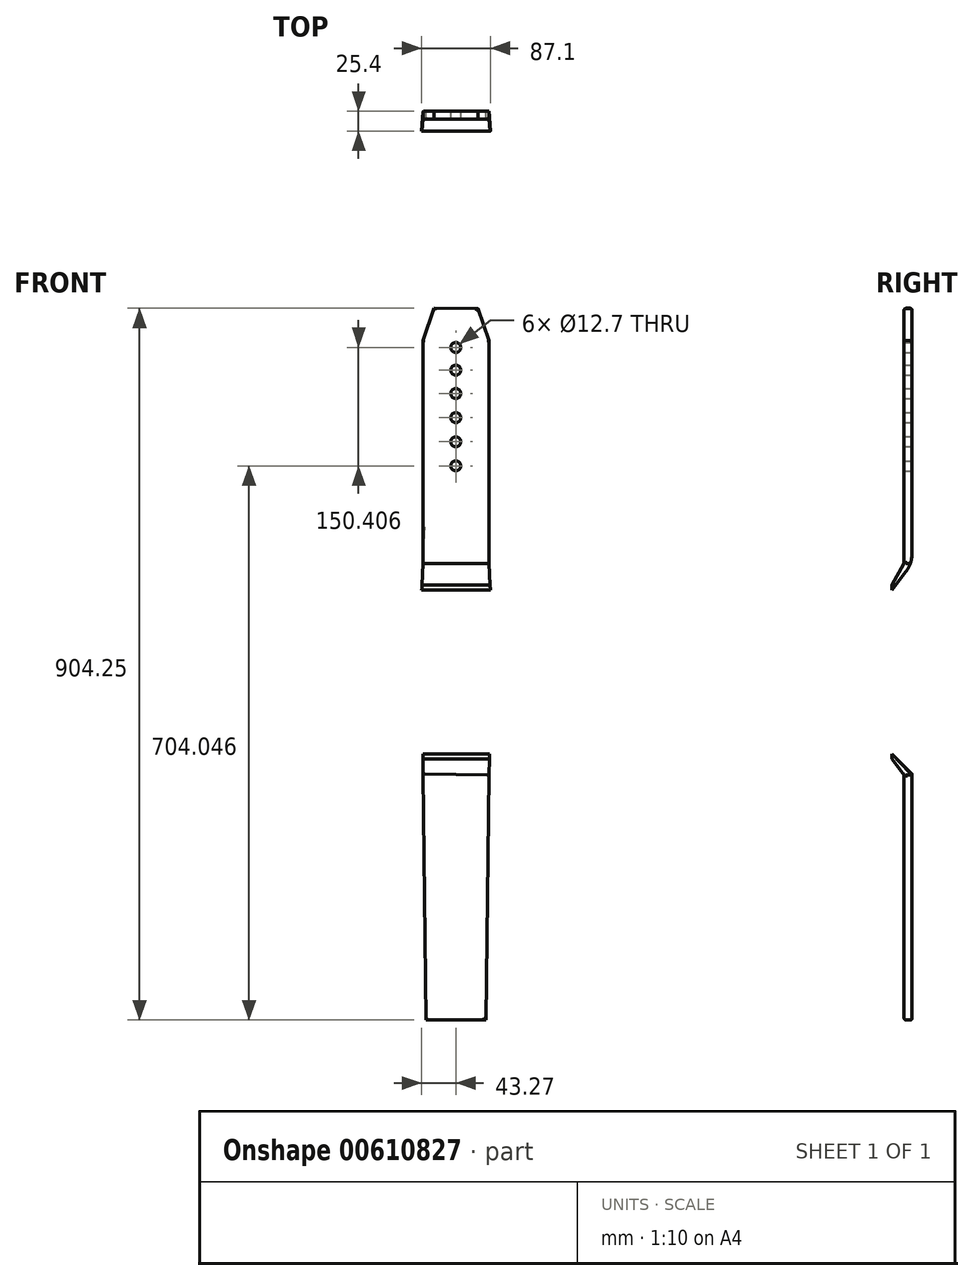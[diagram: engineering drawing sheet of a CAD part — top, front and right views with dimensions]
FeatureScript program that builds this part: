
annotation { "Feature Type Name" : "Feature", "Feature Type Description" : "" }
export const myFeature = defineFeature(function(context is Context, id is Id, definition is map)
    precondition{}
    {
        {
            var Q0;
            Q0=qCreatedBy(makeId("Front.planeOp"),FACE);
            cPlane(context, id + "F0", {"entities" : qUnion([Q0]), "cplaneType" : CPlaneType.OFFSET, "offset" : 17.78 * mm, "oppositeDirection" : true, "width" : 152.4 * mm, "height" : 152.4 * mm});
        }
        {
            var Q0;
            Q0=qCreatedBy(id+"F0.planeOp",FACE);
            var sketch = newSketch(context, id + "F1", { "sketchPlane" : qUnion([Q0])});
            skLineSegment(sketch, "E0.0", {"start": v(-43.1, 101.93) * mm, "end": v(43.66, 101.93) * mm});
            skFitSpline(sketch, "E1.0", {"points": [v(43.66, 101.93) * mm, v(43.72, 99.53) * mm, v(43.79, 97.13) * mm, v(43.86, 94.73) * mm]});
            skLineSegment(sketch, "E2.0", {"start": v(43.83, 95.64) * mm, "end": v(-43.27, 95.64) * mm});
            skFitSpline(sketch, "E3.0", {"points": [v(-43.3, 94.73) * mm, v(-43.22, 97.13) * mm, v(-43.16, 99.53) * mm, v(-43.1, 101.93) * mm]});
            skLineSegment(sketch, "E4.0", {"start": v(42.54, -118.99) * mm, "end": v(-41.97, -118.99) * mm});
            skLineSegment(sketch, "E5.0", {"start": v(-41.97, -112.7) * mm, "end": v(42.54, -112.7) * mm});
            skLineSegment(sketch, "E6.0", {"start": v(-41.97, -118.99) * mm, "end": v(-41.97, -112.7) * mm});
            skLineSegment(sketch, "E7.0", {"start": v(42.54, -112.7) * mm, "end": v(42.54, -118.99) * mm});
            skSolve(sketch);
        }
        {
            var Q0;
            Q0=qCreatedBy(id+"F0.planeOp",FACE);
            cPlane(context, id + "F2", {"entities" : qUnion([Q0]), "cplaneType" : CPlaneType.OFFSET, "offset" : 25.4 * mm, "oppositeDirection" : true, "width" : 152.4 * mm, "height" : 152.4 * mm});
        }
        {
            var Q0;
            Q0=qCreatedBy(id+"F2.planeOp",FACE);
            var sketch = newSketch(context, id + "F3", { "sketchPlane" : qUnion([Q0])});
            skLineSegment(sketch, "E8", {"start": v(42.35, 129.12) * mm, "end": v(-41.73, 129.12) * mm});
            skPoint(sketch, "E9.end.orphan", {"position": v(33.41, 331.77) * mm});
            skPoint(sketch, "E10.end.orphan", {"position": v(-33.96, 331.77) * mm});
            skLineSegment(sketch, "E11", {"start": v(0, 453.24) * mm, "end": v(-27.94, 453.36) * mm});
            skLineSegment(sketch, "E12", {"start": v(-27.94, 453.36) * mm, "end": v(0, 453.24) * mm});
            skLineSegment(sketch, "E13", {"start": v(0, 453.24) * mm, "end": v(27.94, 453.13) * mm});
            skLineSegment(sketch, "E14", {"start": v(42.35, 129.12) * mm, "end": v(42.35, 412.45) * mm});
            skLineSegment(sketch, "E15", {"start": v(-41.73, 129.12) * mm, "end": v(-41.73, 412.45) * mm});
            skLineSegment(sketch, "E16", {"start": v(27.94, 453.13) * mm, "end": v(42.35, 412.45) * mm});
            skLineSegment(sketch, "E17", {"start": v(-27.94, 453.36) * mm, "end": v(-41.73, 412.45) * mm});
            skSolve(sketch);
        }
        {
            var Q0;
            Q0 = qSketchRegion(id + "F3", true);
            extrude(context, id + "F4", {"entities" : qUnion([Q0]), "depth" : 10.16 * mm, "offsetDistance" : 25.4 * mm});
        }
        {
            var Q1;
            Q1=makeQuery(id+"F1.imprint","IMPRINT",FACE,{"disambiguationData":[TD([[makeQuery(id+"F1.imprint","IMPRINT",EDGE,{"derivedFrom":sQuery(id+"F1.wireOp",EDGE,"E0.0")}),-1.0]])]});
            var Q2;
            Q2=makeQuery(id+"F4.opExtrude","SWEPT_FACE",FACE,{"disambiguationData":[OSD([sQuery(id+"F3.wireOp",EDGE,"E8")])]});
            loft(context, id + "F5", {"operationType" : NewBodyOperationType.ADD, "sheetProfilesArray" : [{ "sheetProfileEntities" : qUnion([Q1]) }, { "sheetProfileEntities" : qUnion([Q2]) }]});
        }
        {
            var Q0;
            Q0=qCreatedBy(id+"F2.planeOp",FACE);
            var sketch = newSketch(context, id + "F6", { "sketchPlane" : qUnion([Q0])});
            skLineSegment(sketch, "E18", {"start": v(0, -450.9) * mm, "end": v(-38.1, -450.9) * mm});
            skLineSegment(sketch, "E19", {"start": v(0, -450.9) * mm, "end": v(38.1, -450.9) * mm});
            skLineSegment(sketch, "E20", {"start": v(38.1, -450.9) * mm, "end": v(42.2, -139.38) * mm});
            skLineSegment(sketch, "E21", {"start": v(-38.1, -450.9) * mm, "end": v(-41.68, -138.27) * mm});
            skLineSegment(sketch, "E22", {"start": v(42.2, -139.38) * mm, "end": v(-41.97, -138.27) * mm});
            skPoint(sketch, "E23.0.start.orphan", {"position": v(-41.97, -112.7) * mm});
            skSolve(sketch);
        }
        {
            var Q0;
            Q0 = qSketchRegion(id + "F6", true);
            extrude(context, id + "F7", {"entities" : qUnion([Q0]), "depth" : 10.16 * mm, "offsetDistance" : 25.4 * mm});
        }
        {
            var Q1;
            Q1=makeQuery(id+"F1.imprint","IMPRINT",FACE,{"disambiguationData":[TD([[makeQuery(id+"F1.imprint","IMPRINT",EDGE,{"derivedFrom":sQuery(id+"F1.wireOp",EDGE,"E4.0")}),-1.0]])]});
            var Q2;
            Q2=makeQuery(id+"F7.opExtrude","SWEPT_FACE",FACE,{"disambiguationData":[OSD([sQuery(id+"F6.wireOp",EDGE,"E22")])]});
            loft(context, id + "F8", {"operationType" : NewBodyOperationType.ADD, "sheetProfilesArray" : [{ "sheetProfileEntities" : qUnion([Q1]) }, { "sheetProfileEntities" : qUnion([Q2]) }]});
        }
        {
            var Q0;
            Q0=qCreatedBy(id+"F2.planeOp",FACE);
            var sketch = newSketch(context, id + "F9", { "sketchPlane" : qUnion([Q0])});
            skCircle(sketch, "E24", {"center": v(0, 403.56) * mm, "radius": 6.35 * mm});
            skCircle(sketch, "E25", {"center": v(0, 374.78) * mm, "radius": 6.35 * mm});
            skCircle(sketch, "E26", {"center": v(0, 345.07) * mm, "radius": 6.35 * mm});
            skCircle(sketch, "E27", {"center": v(0, 314.43) * mm, "radius": 6.35 * mm});
            skCircle(sketch, "E28", {"center": v(0, 283.8) * mm, "radius": 6.35 * mm});
            skCircle(sketch, "E29", {"center": v(0, 253.16) * mm, "radius": 6.35 * mm});
            skSolve(sketch);
        }
        {
            var Q0;
            Q0 = qSketchRegion(id + "F9", true);
            extrude(context, id + "F10", {"entities" : qUnion([Q0]), "operationType" : NewBodyOperationType.REMOVE, "depth" : 25.4 * mm, "offsetDistance" : 25.4 * mm});
        }
        {
            var Q0;
            Q0=makeQuery(id+"F4.opExtrude","CAP_EDGE",EDGE,{"disambiguationData":[OSD([sQuery(id+"F3.wireOp",EDGE,"E15")])],"isStart":false});
            var Q1;
            Q1=makeQuery(id+"F4.opExtrude","CAP_EDGE",EDGE,{"disambiguationData":[OSD([sQuery(id+"F3.wireOp",EDGE,"E17")])],"isStart":false});
            var Q2;
            Q2=makeQuery(id+"F4.opExtrude","CAP_EDGE",EDGE,{"disambiguationData":[OSD([sQuery(id+"F3.wireOp",EDGE,"E12"),sQuery(id+"F3.wireOp",EDGE,"E13")])],"isStart":false});
            var Q3;
            Q3=makeQuery(id+"F4.opExtrude","CAP_EDGE",EDGE,{"disambiguationData":[OSD([sQuery(id+"F3.wireOp",EDGE,"E16")])],"isStart":false});
            var Q4;
            Q4=makeQuery(id+"F4.opExtrude","CAP_EDGE",EDGE,{"disambiguationData":[OSD([sQuery(id+"F3.wireOp",EDGE,"E14")])],"isStart":false});
            var Q5;
            Q5=makeQuery(id+"F7.opExtrude","CAP_EDGE",EDGE,{"disambiguationData":[OSD([sQuery(id+"F6.wireOp",EDGE,"E21")])],"isStart":true});
            var Q6;
            Q6=makeQuery(id+"F7.opExtrude","CAP_EDGE",EDGE,{"disambiguationData":[OSD([sQuery(id+"F6.wireOp",EDGE,"E20")])],"isStart":false});
            var Q7;
            Q7=makeQuery(id+"F7.opExtrude","CAP_EDGE",EDGE,{"disambiguationData":[OSD([sQuery(id+"F6.wireOp",EDGE,"E18"),sQuery(id+"F6.wireOp",EDGE,"E19")])],"isStart":false});
            var Q8;
            Q8=makeQuery(id+"F7.opExtrude","CAP_EDGE",EDGE,{"disambiguationData":[OSD([sQuery(id+"F6.wireOp",EDGE,"E21")])],"isStart":false});
            var Q9;
            Q9=makeQuery(id+"F4.opExtrude","CAP_EDGE",EDGE,{"disambiguationData":[OSD([sQuery(id+"F3.wireOp",EDGE,"E15")])],"isStart":true});
            var Q10;
            Q10=makeQuery(id+"F4.opExtrude","CAP_EDGE",EDGE,{"disambiguationData":[OSD([sQuery(id+"F3.wireOp",EDGE,"E17")])],"isStart":true});
            var Q11;
            Q11=makeQuery(id+"F4.opExtrude","CAP_EDGE",EDGE,{"disambiguationData":[OSD([sQuery(id+"F3.wireOp",EDGE,"E16")])],"isStart":true});
            var Q12;
            Q12=makeQuery(id+"F4.opExtrude","CAP_EDGE",EDGE,{"disambiguationData":[OSD([sQuery(id+"F3.wireOp",EDGE,"E12"),sQuery(id+"F3.wireOp",EDGE,"E13")])],"isStart":true});
            var Q13;
            Q13=makeQuery(id+"F7.opExtrude","CAP_EDGE",EDGE,{"disambiguationData":[OSD([sQuery(id+"F6.wireOp",EDGE,"E20")])],"isStart":true});
            var Q14;
            Q14=makeQuery(id+"F7.opExtrude","CAP_EDGE",EDGE,{"disambiguationData":[OSD([sQuery(id+"F6.wireOp",EDGE,"E18"),sQuery(id+"F6.wireOp",EDGE,"E19")])],"isStart":true});
            fillet(context, id + "F11", {"entities" : qUnion([Q0, Q1, Q2, Q3, Q4, Q5, Q6, Q7, Q8, Q9, Q10, Q11, Q12, Q13, Q14]), "radius" : 2.54 * mm, "tangentPropagation" : true, "allowEdgeOverflow" : false});
        }
        {
            var Q0;
            {var subQ0=sQuery(id+"F3.wireOp",EDGE,"E8");var subQ1=makeQuery(id+"F4.opExtrude","CAP_EDGE",EDGE,{"disambiguationData":[OSD([subQ0])],"isStart":true});var subQ2=sQuery(id+"F3.wireOp",EDGE,"E15");var subQ3=sQuery(id+"F3.wireOp",EDGE,"E14");Q0=makeQuery(id+"F5.boolean.opBoolean","MERGE",EDGE,{"derivedFrom":[subQ1,makeQuery(id+"F5.opLoft","MID_CAP_EDGE",EDGE,{"disambiguationData":[OSD([subQ0,subQ3,subQ2]),TDD([makeQuery(id+"F4.opExtrude","CAP_VERTEX",VERTEX,{"disambiguationData":[OSD([subQ0,subQ3])],"isStart":true}),makeQuery(id+"F4.opExtrude","CAP_VERTEX",VERTEX,{"disambiguationData":[OSD([subQ0,subQ2])],"isStart":true}),subQ1])],"capPos":1.0})]});}
            var Q1;
            {var subQ0=sQuery(id+"F6.wireOp",EDGE,"E22");var subQ1=makeQuery(id+"F7.opExtrude","CAP_EDGE",EDGE,{"disambiguationData":[OSD([subQ0])],"isStart":true});var subQ2=sQuery(id+"F6.wireOp",EDGE,"E21");var subQ3=sQuery(id+"F6.wireOp",EDGE,"E20");Q1=makeQuery(id+"F8.boolean.opBoolean","MERGE",EDGE,{"derivedFrom":[subQ1,makeQuery(id+"F8.opLoft","MID_CAP_EDGE",EDGE,{"disambiguationData":[OSD([subQ3,subQ2,subQ0]),TDD([makeQuery(id+"F7.opExtrude","CAP_VERTEX",VERTEX,{"disambiguationData":[OSD([subQ3,subQ0])],"isStart":true}),makeQuery(id+"F7.opExtrude","CAP_VERTEX",VERTEX,{"disambiguationData":[OSD([subQ2,subQ0])],"isStart":true}),subQ1])],"capPos":1.0})]});}
            fillet(context, id + "F12", {"entities" : qUnion([Q0, Q1]), "radius" : 38.1 * mm, "tangentPropagation" : true, "allowEdgeOverflow" : false});
        }
    });
